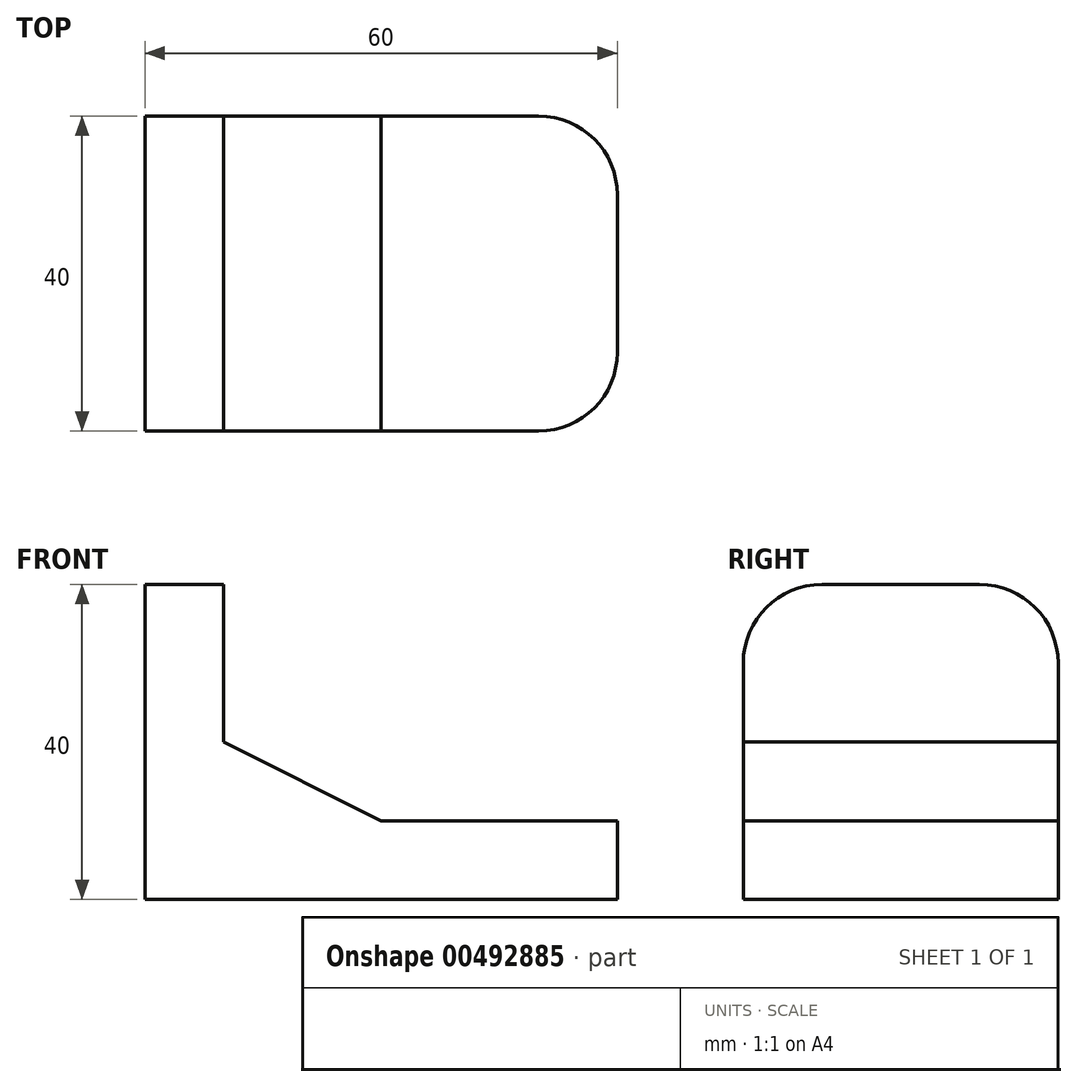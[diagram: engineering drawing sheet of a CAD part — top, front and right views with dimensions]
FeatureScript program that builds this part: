
annotation { "Feature Type Name" : "Feature", "Feature Type Description" : "" }
export const myFeature = defineFeature(function(context is Context, id is Id, definition is map)
    precondition{}
    {
        {
            var Q0;
            Q0=qCreatedBy(makeId("Front.planeOp"),FACE);
            var sketch = newSketch(context, id + "F0", { "sketchPlane" : qUnion([Q0])});
            skLineSegment(sketch, "E0", {"start": v(0, 0) * mm, "end": v(0, 40) * mm});
            skLineSegment(sketch, "E1", {"start": v(0, 40) * mm, "end": v(10, 40) * mm});
            skLineSegment(sketch, "E2", {"start": v(10, 40) * mm, "end": v(10, 20) * mm});
            skLineSegment(sketch, "E3", {"start": v(10, 20) * mm, "end": v(30, 10) * mm});
            skLineSegment(sketch, "E4", {"start": v(30, 10) * mm, "end": v(60, 10) * mm});
            skLineSegment(sketch, "E5", {"start": v(60, 10) * mm, "end": v(60, 0) * mm});
            skLineSegment(sketch, "E6", {"start": v(60, 0) * mm, "end": v(0, 0) * mm});
            skSolve(sketch);
        }
        {
            var Q0;
            Q0=makeQuery(id+"F0.imprint","IMPRINT",FACE,{"disambiguationData":[TD([[makeQuery(id+"F0.imprint","IMPRINT",EDGE,{"derivedFrom":sQuery(id+"F0.wireOp",EDGE,"E0")}),-1.0]])]});
            extrude(context, id + "F1", {"entities" : qUnion([Q0]), "depth" : 40 * mm});
        }
        {
            var Q0;
            Q0=makeQuery(id+"F1.opExtrude","CAP_EDGE",EDGE,{"disambiguationData":[OSD([sQuery(id+"F0.wireOp",EDGE,"E1")])],"isStart":false});
            var Q1;
            Q1=makeQuery(id+"F1.opExtrude","CAP_EDGE",EDGE,{"disambiguationData":[OSD([sQuery(id+"F0.wireOp",EDGE,"E5")])],"isStart":false});
            var Q2;
            Q2=makeQuery(id+"F1.opExtrude","CAP_EDGE",EDGE,{"disambiguationData":[OSD([sQuery(id+"F0.wireOp",EDGE,"E5")])],"isStart":true});
            var Q3;
            Q3=makeQuery(id+"F1.opExtrude","CAP_EDGE",EDGE,{"disambiguationData":[OSD([sQuery(id+"F0.wireOp",EDGE,"E1")])],"isStart":true});
            fillet(context, id + "F2", {"entities" : qUnion([Q0, Q1, Q2, Q3]), "radius" : 10 * mm, "tangentPropagation" : true, "allowEdgeOverflow" : false});
        }
    });
